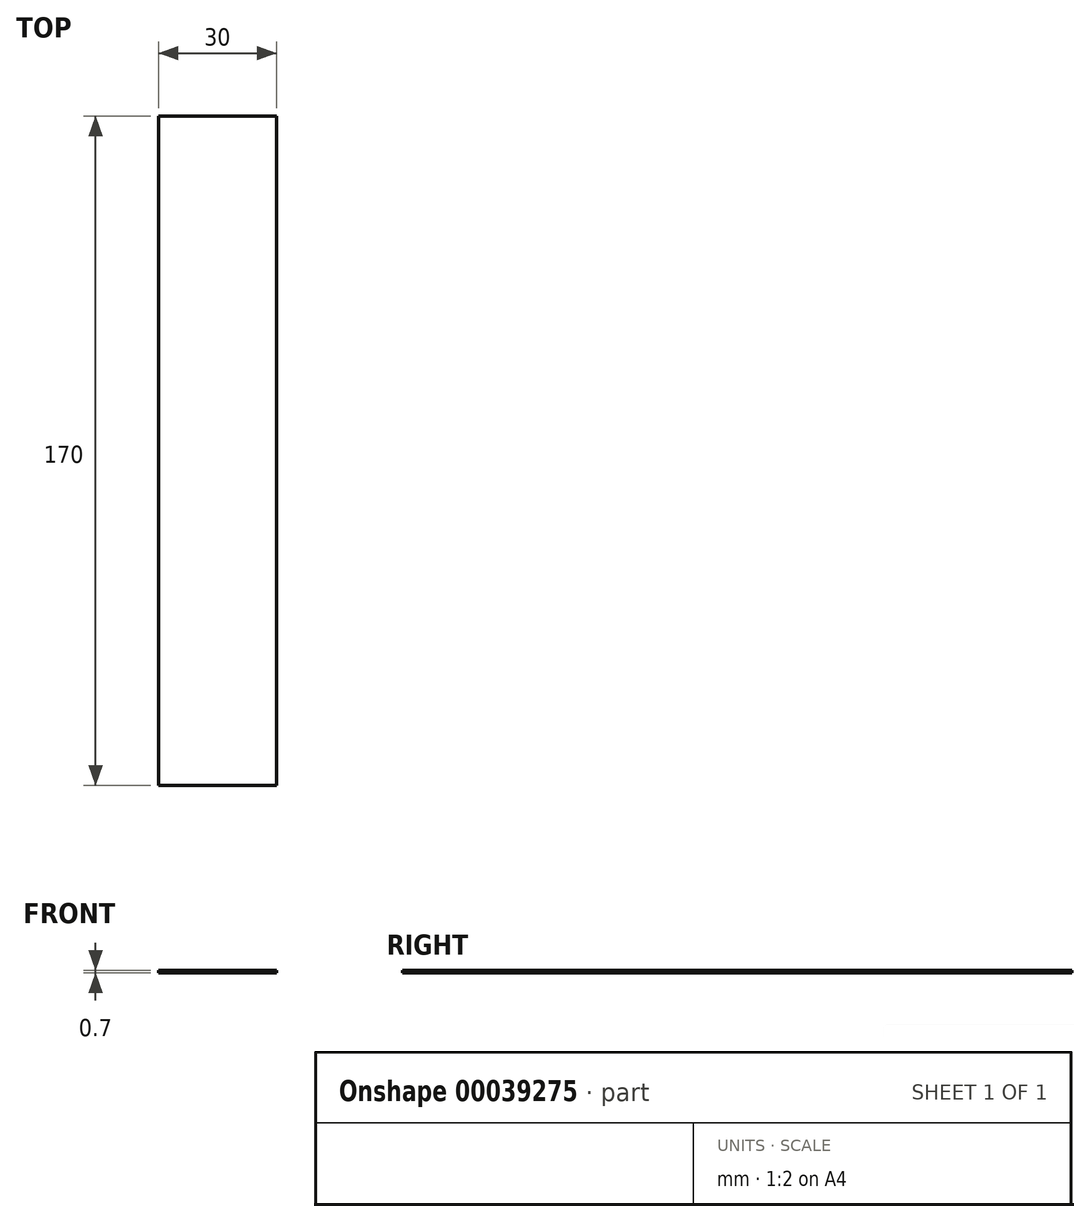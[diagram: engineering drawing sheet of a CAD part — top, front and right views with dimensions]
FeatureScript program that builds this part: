
annotation { "Feature Type Name" : "Feature", "Feature Type Description" : "" }
export const myFeature = defineFeature(function(context is Context, id is Id, definition is map)
    precondition{}
    {
        {
            var Q0;
            Q0=qCreatedBy(makeId("Top.planeOp"),FACE);
            var sketch = newSketch(context, id + "F0", { "sketchPlane" : qUnion([Q0])});
            skLineSegment(sketch, "E0.bottom", {"start": v(0, 0) * mm, "end": v(30, 0) * mm});
            skLineSegment(sketch, "E0.top", {"start": v(0, -170) * mm, "end": v(30, -170) * mm});
            skLineSegment(sketch, "E0.left", {"start": v(0, 0) * mm, "end": v(0, -170) * mm});
            skLineSegment(sketch, "E0.right", {"start": v(30, 0) * mm, "end": v(30, -170) * mm});
            skSolve(sketch);
        }
        {
            var Q0;
            Q0 = qSketchRegion(id + "F0", true);
            extrude(context, id + "F1", {"entities" : qUnion([Q0]), "depth" : 0.7 * mm});
        }
    });
